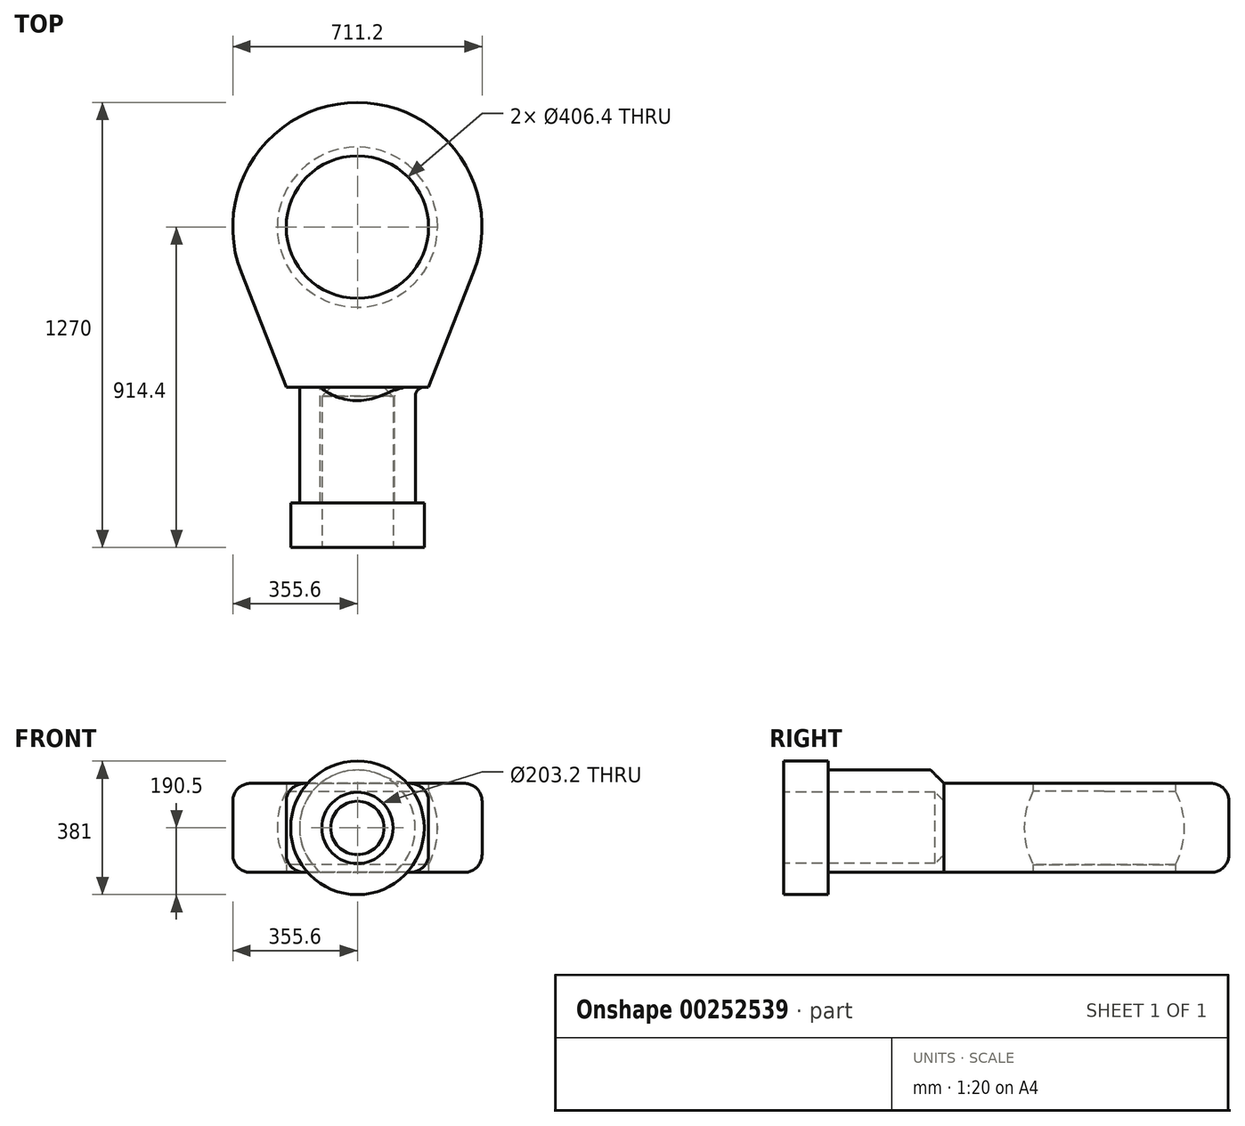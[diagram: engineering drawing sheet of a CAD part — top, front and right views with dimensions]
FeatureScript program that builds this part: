
annotation { "Feature Type Name" : "Feature", "Feature Type Description" : "" }
export const myFeature = defineFeature(function(context is Context, id is Id, definition is map)
    precondition{}
    {
        {
            var Q0;
            Q0=qCreatedBy(makeId("Top.planeOp"),FACE);
            var sketch = newSketch(context, id + "F0", { "sketchPlane" : qUnion([Q0])});
            skArc(sketch, "E0", {"start": v(331.24, -129.36) * mm, "mid": v(0, 355.6) * mm, "end": v(-331.24, -129.36) * mm});
            skCircle(sketch, "E1", {"center": v(0, 0) * mm, "radius": 203.2 * mm});
            skLineSegment(sketch, "E2", {"start": v(-203.2, -457.2) * mm, "end": v(203.2, -457.2) * mm});
            skLineSegment(sketch, "E3", {"start": v(-203.2, -457.2) * mm, "end": v(-331.24, -129.36) * mm});
            skLineSegment(sketch, "E4", {"start": v(331.24, -129.36) * mm, "end": v(203.2, -457.2) * mm});
            skPoint(sketch, "E5.trimOffspring.end.orphan", {"position": v(0, -457.2) * mm});
            skSolve(sketch);
        }
        {
            var Q0;
            Q0=makeQuery(id+"F0.imprint","IMPRINT",FACE,{"disambiguationData":[TD([[makeQuery(id+"F0.imprint","IMPRINT",EDGE,{"derivedFrom":sQuery(id+"F0.wireOp",EDGE,"E0")}),1.0]])]});
            extrude(context, id + "F1", {"entities" : qUnion([Q0]), "depth" : 254 * mm});
        }
        {
            var Q0;
            Q0=qCreatedBy(makeId("Right.planeOp"),FACE);
            var sketch = newSketch(context, id + "F2", { "sketchPlane" : qUnion([Q0])});
            skLineSegment(sketch, "E6", {"start": v(0, 0) * mm, "end": v(0, 254) * mm});
            skPoint(sketch, "E7", {"position": v(0, 127) * mm});
            skArc(sketch, "E8", {"start": v(-190.08, 254) * mm, "mid": v(-228.6, 127) * mm, "end": v(-190.08, 0) * mm});
            skLineSegment(sketch, "E9", {"start": v(190.08, 0) * mm, "end": v(-190.08, 0) * mm});
            skLineSegment(sketch, "E10", {"start": v(0, 254) * mm, "end": v(-190.08, 254) * mm});
            skLineSegment(sketch, "E11", {"start": v(-190.08, 254) * mm, "end": v(190.08, 254) * mm});
            skArc(sketch, "E12.trimOffspring", {"start": v(190.08, 0) * mm, "mid": v(228.6, 127) * mm, "end": v(190.08, 254) * mm});
            skSolve(sketch);
        }
        {
            var Q0;
            {var subQ0=sQuery(id+"F2.wireOp",EDGE,"E6");Q0=makeQuery(id+"F2.imprint","IMPRINT",FACE,{"disambiguationData":[TD([[makeQuery(id+"F2.imprint","IMPRINT",EDGE,{"derivedFrom":subQ0}),1.0]])]});}
            var Q1;
            Q1=sQuery(id+"F2.wireOp",EDGE,"E6");
            revolve(context, id + "F3", {"operationType" : NewBodyOperationType.REMOVE, "entities" : qUnion([Q0]), "axis" : qUnion([Q1]), "revolveType" : RevolveType.FULL, "oppositeDirection" : true});
        }
        {
            var Q0;
            Q0=makeQuery(id+"F1.opExtrude","SWEPT_FACE",FACE,{"disambiguationData":[OSD([sQuery(id+"F0.wireOp",EDGE,"E0")])]});
            fillet(context, id + "F4", {"entities" : qUnion([Q0]), "radius" : 50.8 * mm, "tangentPropagation" : true, "allowEdgeOverflow" : false});
        }
        {
            var Q0;
            Q0=makeQuery(id+"F1.opExtrude","SWEPT_FACE",FACE,{"disambiguationData":[OSD([sQuery(id+"F0.wireOp",EDGE,"E2")])]});
            var sketch = newSketch(context, id + "F5", { "sketchPlane" : qUnion([Q0])});
            skPoint(sketch, "E13", {"position": v(0, 254) * mm});
            skPoint(sketch, "E14", {"position": v(0, 0) * mm});
            skPoint(sketch, "E15", {"position": v(-203.2, 127) * mm});
            skPoint(sketch, "E16", {"position": v(0, 127) * mm});
            skCircle(sketch, "E17", {"center": v(0, 127) * mm, "radius": 165.1 * mm});
            skSolve(sketch);
        }
        {
            var Q0;
            {var subQ0=sQuery(id+"F5.wireOp",EDGE,"E17");var subQ1=sQuery(id+"F0.wireOp",EDGE,"E2");var subQ2=makeQuery(id+"F1.opExtrude","CAP_EDGE",EDGE,{"disambiguationData":[OSD([subQ1])],"isStart":false});var subQ3=makeQuery(id+"F5.imprint","INTERSECT",VERTEX,{"disambiguationData":[OD(0.0)],"derivedFrom":[subQ2,subQ0]});Q0=makeQuery(id+"F5.imprint","IMPRINT",FACE,{"disambiguationData":[TD([[makeQuery(id+"F5.imprint","IMPRINT",EDGE,{"disambiguationData":[TD([[subQ3,-1.0]])],"derivedFrom":subQ0}),1.0]])]});}
            var Q1;
            {var subQ0=sQuery(id+"F5.wireOp",EDGE,"E17");var subQ1=makeQuery(id+"F1.opExtrude","CAP_EDGE",EDGE,{"disambiguationData":[OSD([sQuery(id+"F0.wireOp",EDGE,"E2")])],"isStart":false});var subQ2=makeQuery(id+"F5.imprint","INTERSECT",VERTEX,{"disambiguationData":[OD(0.0)],"derivedFrom":[subQ1,subQ0]});Q1=makeQuery(id+"F5.imprint","IMPRINT",FACE,{"disambiguationData":[TD([[makeQuery(id+"F5.imprint","IMPRINT",EDGE,{"disambiguationData":[TD([[subQ2,1.0]])],"derivedFrom":subQ0}),1.0]])]});}
            var Q2;
            {var subQ0=sQuery(id+"F5.wireOp",EDGE,"E17");var subQ1=makeQuery(id+"F1.opExtrude","CAP_EDGE",EDGE,{"disambiguationData":[OSD([sQuery(id+"F0.wireOp",EDGE,"E2")])],"isStart":true});var subQ2=makeQuery(id+"F5.imprint","INTERSECT",VERTEX,{"disambiguationData":[OD(0.0)],"derivedFrom":[subQ1,subQ0]});Q2=makeQuery(id+"F5.imprint","IMPRINT",FACE,{"disambiguationData":[TD([[makeQuery(id+"F5.imprint","IMPRINT",EDGE,{"disambiguationData":[TD([[subQ2,-1.0]])],"derivedFrom":subQ0}),1.0]])]});}
            extrude(context, id + "F6", {"entities" : qUnion([Q0, Q1, Q2]), "operationType" : NewBodyOperationType.ADD, "depth" : 330.2 * mm});
        }
        {
            var Q0;
            Q0=makeQuery(id+"F6.opExtrude","CAP_FACE",FACE,{"disambiguationData":[OSD([sQuery(id+"F5.wireOp",EDGE,"E17")])],"isStart":false});
            var sketch = newSketch(context, id + "F7", { "sketchPlane" : qUnion([Q0])});
            skCircle(sketch, "E18", {"center": v(0, 127) * mm, "radius": 190.5 * mm});
            skSolve(sketch);
        }
        {
            var Q0;
            Q0=makeQuery(id+"F7.imprint","IMPRINT",FACE,{"disambiguationData":[TD([[makeQuery(id+"F7.imprint","IMPRINT",EDGE,{"derivedFrom":sQuery(id+"F7.wireOp",EDGE,"E18")}),1.0]])]});
            var Q1;
            Q1=makeQuery(id+"F7.imprint","IMPRINT",FACE,{"disambiguationData":[TD([[makeQuery(id+"F7.imprint","IMPRINT",EDGE,{"derivedFrom":makeQuery(id+"F6.opExtrude","CAP_EDGE",EDGE,{"disambiguationData":[OSD([sQuery(id+"F5.wireOp",EDGE,"E17")])],"isStart":false})}),1.0]])]});
            extrude(context, id + "F8", {"entities" : qUnion([Q0, Q1]), "operationType" : NewBodyOperationType.ADD, "depth" : 127 * mm});
        }
        {
            var Q0;
            {var subQ0=sQuery(id+"F5.wireOp",EDGE,"E17");Q0=makeQuery(id+"F6.boolean.opBoolean","SPLIT",EDGE,{"disambiguationData":[topologyDisambiguationEdgeConnected([makeQuery(id+"F1.opExtrude","SWEPT_FACE",FACE,{"disambiguationData":[OSD([sQuery(id+"F0.wireOp",EDGE,"E2")])]}),makeQuery(id+"F6.opExtrude","SWEPT_FACE",FACE,{"disambiguationData":[OSD([subQ0])]})]),OD(1.0)],"derivedFrom":makeQuery(id+"F6.opExtrude","CAP_EDGE",EDGE,{"disambiguationData":[OSD([subQ0])],"isStart":true})});}
            var Q1;
            {var subQ0=sQuery(id+"F5.wireOp",EDGE,"E17");Q1=makeQuery(id+"F6.boolean.opBoolean","SPLIT",EDGE,{"disambiguationData":[topologyDisambiguationEdgeConnected([makeQuery(id+"F1.opExtrude","SWEPT_FACE",FACE,{"disambiguationData":[OSD([sQuery(id+"F0.wireOp",EDGE,"E2")])]}),makeQuery(id+"F6.opExtrude","SWEPT_FACE",FACE,{"disambiguationData":[OSD([subQ0])]})]),OD(0.0)],"derivedFrom":makeQuery(id+"F6.opExtrude","CAP_EDGE",EDGE,{"disambiguationData":[OSD([subQ0])],"isStart":true})});}
            fillet(context, id + "F9", {"entities" : qUnion([Q0, Q1]), "radius" : 25.4 * mm, "tangentPropagation" : true, "allowEdgeOverflow" : false});
        }
        {
            var Q0;
            {var subQ0=sQuery(id+"F0.wireOp",EDGE,"E2");var subQ1=sQuery(id+"F5.wireOp",EDGE,"E17");Q0=makeQuery(id+"F6.boolean.opBoolean","SPLIT",FACE,{"disambiguationData":[TD([makeQuery(id+"F1.opExtrude","CAP_FACE",FACE,{"disambiguationData":[OSD([sQuery(id+"F0.wireOp",EDGE,"E0"),sQuery(id+"F0.wireOp",EDGE,"E1"),subQ0,sQuery(id+"F0.wireOp",EDGE,"E3"),sQuery(id+"F0.wireOp",EDGE,"E4")])],"isStart":false})])],"derivedFrom":makeQuery(id+"F6.opExtrude","CAP_FACE",FACE,{"disambiguationData":[OSD([subQ1])],"isStart":true})});}
            var Q1;
            {var subQ0=sQuery(id+"F0.wireOp",EDGE,"E2");var subQ1=sQuery(id+"F5.wireOp",EDGE,"E17");Q1=makeQuery(id+"F6.boolean.opBoolean","SPLIT",FACE,{"disambiguationData":[TD([makeQuery(id+"F1.opExtrude","CAP_FACE",FACE,{"disambiguationData":[OSD([sQuery(id+"F0.wireOp",EDGE,"E0"),sQuery(id+"F0.wireOp",EDGE,"E1"),subQ0,sQuery(id+"F0.wireOp",EDGE,"E3"),sQuery(id+"F0.wireOp",EDGE,"E4")])],"isStart":true})])],"derivedFrom":makeQuery(id+"F6.opExtrude","CAP_FACE",FACE,{"disambiguationData":[OSD([subQ1])],"isStart":true})});}
            extrude(context, id + "F10", {"entities" : qUnion([Q0, Q1]), "operationType" : NewBodyOperationType.REMOVE, "oppositeDirection" : true, "depth" : 50.8 * mm});
        }
        {
            var Q0;
            {var subQ0=sQuery(id+"F0.wireOp",EDGE,"E2");Q0=makeQuery(id+"F10.boolean.opBoolean","COPY",EDGE,{"derivedFrom":makeQuery(id+"F10.opExtrude","CAP_EDGE",EDGE,{"disambiguationData":[OSD([subQ0]),TDD([makeQuery(id+"F6.boolean.opBoolean","SPLIT",EDGE,{"disambiguationData":[topologyDisambiguationEdgeConnected([makeQuery(id+"F1.opExtrude","CAP_FACE",FACE,{"disambiguationData":[OSD([sQuery(id+"F0.wireOp",EDGE,"E0"),sQuery(id+"F0.wireOp",EDGE,"E1"),subQ0,sQuery(id+"F0.wireOp",EDGE,"E3"),sQuery(id+"F0.wireOp",EDGE,"E4")])],"isStart":false}),makeQuery(id+"F6.opExtrude","CAP_FACE",FACE,{"disambiguationData":[OSD([sQuery(id+"F5.wireOp",EDGE,"E17")])],"isStart":true})])],"derivedFrom":makeQuery(id+"F1.opExtrude","CAP_EDGE",EDGE,{"disambiguationData":[OSD([subQ0])],"isStart":false})})])],"isStart":false})});}
            var Q1;
            {var subQ0=sQuery(id+"F0.wireOp",EDGE,"E2");Q1=makeQuery(id+"F10.boolean.opBoolean","COPY",EDGE,{"derivedFrom":makeQuery(id+"F10.opExtrude","CAP_EDGE",EDGE,{"disambiguationData":[OSD([subQ0]),TDD([makeQuery(id+"F6.boolean.opBoolean","SPLIT",EDGE,{"disambiguationData":[topologyDisambiguationEdgeConnected([makeQuery(id+"F1.opExtrude","CAP_FACE",FACE,{"disambiguationData":[OSD([sQuery(id+"F0.wireOp",EDGE,"E0"),sQuery(id+"F0.wireOp",EDGE,"E1"),subQ0,sQuery(id+"F0.wireOp",EDGE,"E3"),sQuery(id+"F0.wireOp",EDGE,"E4")])],"isStart":true}),makeQuery(id+"F6.opExtrude","CAP_FACE",FACE,{"disambiguationData":[OSD([sQuery(id+"F5.wireOp",EDGE,"E17")])],"isStart":true})])],"derivedFrom":makeQuery(id+"F1.opExtrude","CAP_EDGE",EDGE,{"disambiguationData":[OSD([subQ0])],"isStart":true})})])],"isStart":false})});}
            chamfer(context, id + "F11", {"entities" : qUnion([Q0, Q1]), "width" : 50.8 * mm, "tangentPropagation" : true});
        }
        {
            var Q0;
            Q0=makeQuery(id+"F8.opExtrude","CAP_FACE",FACE,{"disambiguationData":[OSD([sQuery(id+"F7.wireOp",EDGE,"E18")])],"isStart":false});
            var sketch = newSketch(context, id + "F12", { "sketchPlane" : qUnion([Q0])});
            skPoint(sketch, "E19", {"position": v(0, -63.5) * mm});
            skPoint(sketch, "E20", {"position": v(0, 127) * mm});
            skCircle(sketch, "E21", {"center": v(0, 127) * mm, "radius": 101.6 * mm});
            skSolve(sketch);
        }
        {
            var Q0;
            Q0=makeQuery(id+"F12.imprint","IMPRINT",FACE,{"disambiguationData":[TD([[makeQuery(id+"F12.imprint","IMPRINT",EDGE,{"derivedFrom":sQuery(id+"F12.wireOp",EDGE,"E21")}),1.0]])]});
            extrude(context, id + "F13", {"entities" : qUnion([Q0]), "operationType" : NewBodyOperationType.REMOVE, "oppositeDirection" : true, "depth" : 457.2 * mm});
        }
        {
            var Q0;
            Q0=makeQuery(id+"F13.boolean.opBoolean","COPY",EDGE,{"derivedFrom":makeQuery(id+"F13.opExtrude","CAP_EDGE",EDGE,{"disambiguationData":[OSD([sQuery(id+"F12.wireOp",EDGE,"E21")])],"isStart":false})});
            chamfer(context, id + "F14", {"entities" : qUnion([Q0]), "width" : 25.4 * mm, "tangentPropagation" : true});
        }
    });
